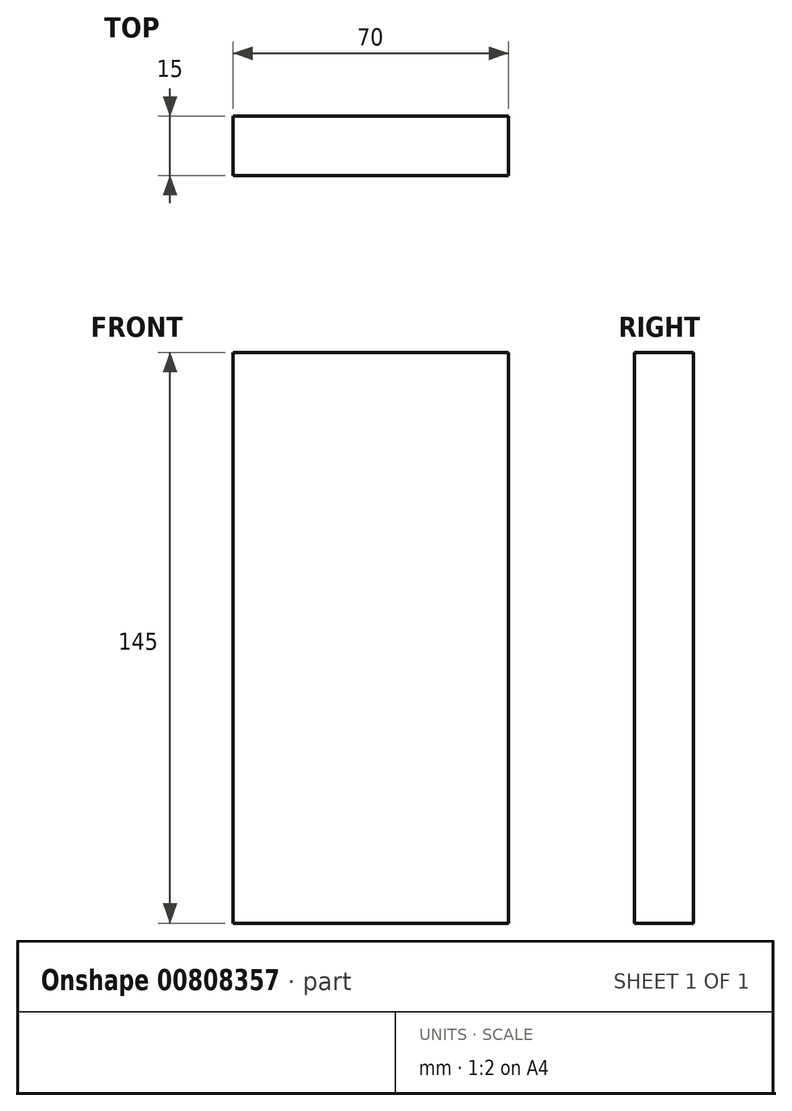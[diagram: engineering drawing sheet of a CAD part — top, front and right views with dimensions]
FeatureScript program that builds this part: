
annotation { "Feature Type Name" : "Feature", "Feature Type Description" : "" }
export const myFeature = defineFeature(function(context is Context, id is Id, definition is map)
    precondition{}
    {
        {
            var Q0;
            Q0=qCreatedBy(makeId("Front.planeOp"),FACE);
            var sketch = newSketch(context, id + "F0", { "sketchPlane" : qUnion([Q0])});
            skLineSegment(sketch, "E0.bottom", {"start": v(35, 72.5) * mm, "end": v(-35, 72.5) * mm});
            skLineSegment(sketch, "E0.top", {"start": v(35, -72.5) * mm, "end": v(-35, -72.5) * mm});
            skLineSegment(sketch, "E0.left", {"start": v(35, 72.5) * mm, "end": v(35, -72.5) * mm});
            skLineSegment(sketch, "E0.right", {"start": v(-35, 72.5) * mm, "end": v(-35, -72.5) * mm});
            skPoint(sketch, "E0.middle", {"position": v(0, 0) * mm});
            skSolve(sketch);
        }
        {
            var Q0;
            Q0=makeQuery(id+"F0.imprint","IMPRINT",FACE,{"disambiguationData":[TD([[makeQuery(id+"F0.imprint","IMPRINT",EDGE,{"derivedFrom":sQuery(id+"F0.wireOp",EDGE,"E0.bottom")}),1.0]])]});
            extrude(context, id + "F1", {"entities" : qUnion([Q0]), "endBound" : BoundingType.SYMMETRIC, "depth" : 15 * mm, "offsetDistance" : 25 * mm});
        }
    });
